# Revit family: Drain_Floor-Jay R.Smith-Round_Type-2108_Series
name_source: partatom
category: Plumbing Fixtures
units: mm (PartAtom-declared; Revit-internal decimal feet)

## family parameters
Always vertical = Yes
Cut with Voids When Loaded = No
OmniClass Number = 23.70.50.21.24
OmniClass Title = Waste Water Drains
Part Type = Normal
Room Calculation Point = No
Round Connector Dimension = Use Diameter
Shared = No
Work Plane-Based = Yes

## types (6) — shared parameters
Assembly Code = D2030300
Body Material = Cast Iron-Jay R Smith-Duco Coated
CW Connection = No
Default Elevation = 0"
Depth Of Body = 4"
Description = Small Capacity General Purpose Floor Drain
Diameter = 9"
FBS - Flat Bottom Strainer = No
G - All Galvanized = No
HW Connection = No
Installation Type = Floor Mounted
L - Speedi-Set Service Weight = No
LXH - Speedi-Set Extra Heavy = No
Load Rating = Light Duty having a Safe Live (Static) Load less than 2,000 lbs. (900 kg) per ASME A112.6.3 Floor Drain Standard.
Manufacturer = Jay R. Smith
NB - Nickel Bronze Top = No
Non-Tilting Grate L/Bucket = No
PB - Polished Bronze Top = No
Product Documentation Link = https://www.jrsmith.com
Product Page URL = https://www.jrsmith.com
Quad Close Trap Seal = No
Side Outlet = No
Strainer Diameter = 7 1/2"
Strainer Height = 1 5/8"
Trap Primer Connection -P050   1/2" (13) & -P075 3/4" (19) = No
URL = http://www.jrsmith.com
Vent Connection = No
Waste Connection = Yes

## per-type parameters (varying)
| type | Connection Description | Distance | Outlet Diameter | Outlet Radius |
| 2108C02 | 2" Caulk Outlet Connection | 1 1/2" | 2" | 1" |
| 2108C03 | 3" Caulk Outlet Connection | 2" | 3" | 1 1/2" |
| 2108C04 | 4" Caulk Outlet Connection | 2 1/2" | 4" | 2" |
| 2108Y02 | 2" No-HUB Outlet Connection | 1 1/2" | 2" | 1" |
| 2108Y03 | 3" No-HUB Outlet Connection | 2" | 3" | 1 1/2" |
| 2108Y04 | 4" No-HUB Outlet Connection | 2 1/2" | 4" | 2" |

note: column(s) folded — value = type name in every type: Model

## geometry (parser evidence)
native form markers: Sweep x3
no freeform markers — native parametric forms only
